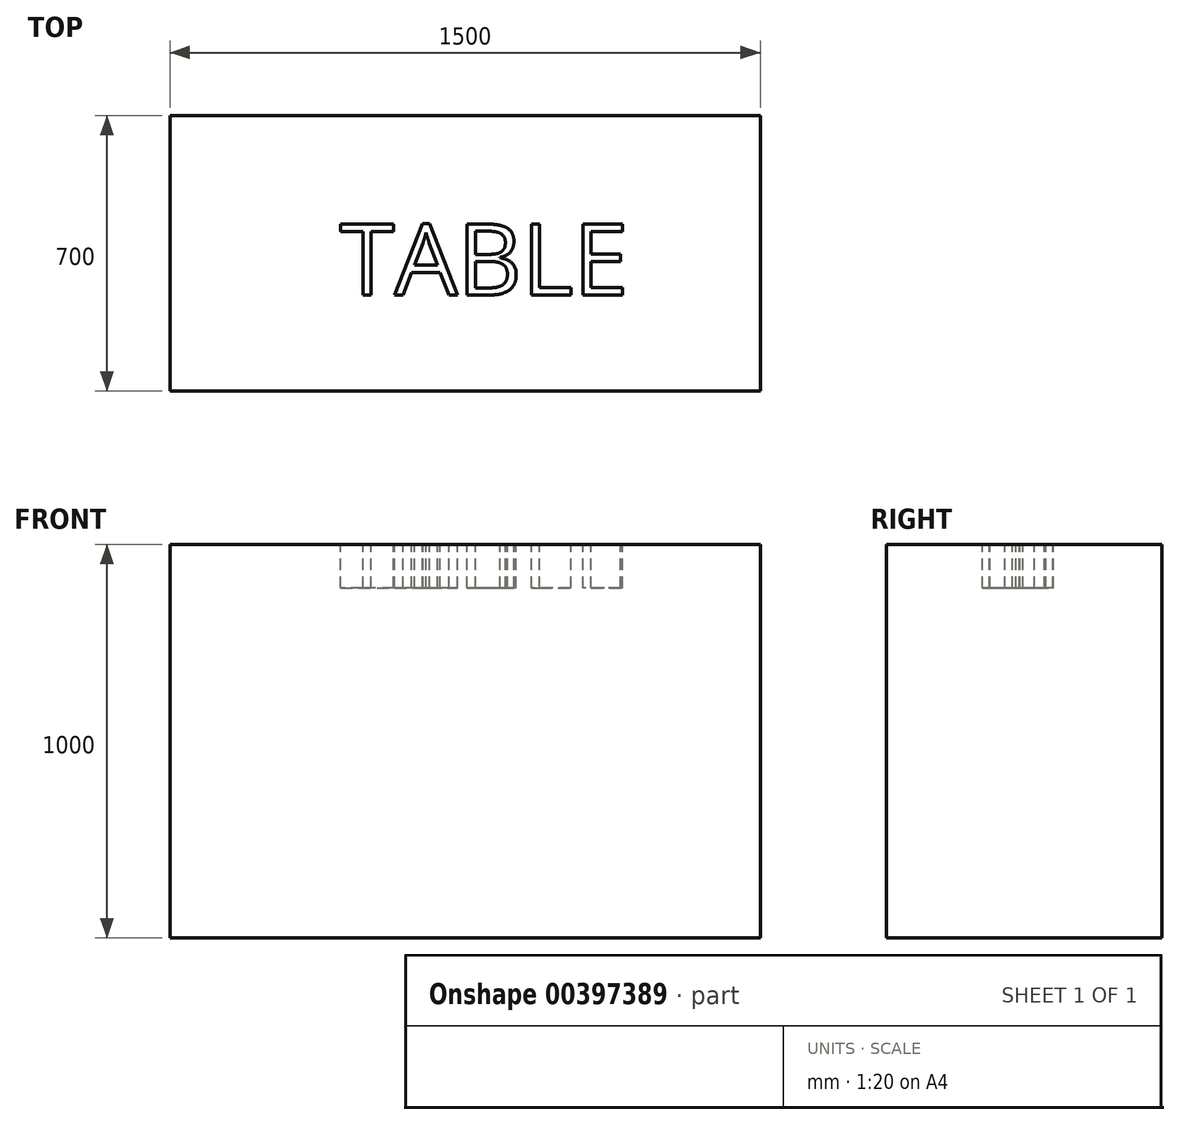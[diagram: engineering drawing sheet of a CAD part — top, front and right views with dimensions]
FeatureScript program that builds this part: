
annotation { "Feature Type Name" : "Feature", "Feature Type Description" : "" }
export const myFeature = defineFeature(function(context is Context, id is Id, definition is map)
    precondition{}
    {
        {
            var Q0;
            Q0=qCreatedBy(makeId("Top.planeOp"),FACE);
            var sketch = newSketch(context, id + "F0", { "sketchPlane" : qUnion([Q0])});
            skLineSegment(sketch, "E0.bottom", {"start": v(-19.1, 693.58) * mm, "end": v(1480.9, 693.58) * mm});
            skLineSegment(sketch, "E0.top", {"start": v(-19.1, -6.42) * mm, "end": v(1480.9, -6.42) * mm});
            skLineSegment(sketch, "E0.left", {"start": v(-19.1, 693.58) * mm, "end": v(-19.1, -6.42) * mm});
            skLineSegment(sketch, "E0.right", {"start": v(1480.9, 693.58) * mm, "end": v(1480.9, -6.42) * mm});
            skSolve(sketch);
        }
        {
            var Q0;
            Q0 = qSketchRegion(id + "F0", true);
            extrude(context, id + "F1", {"entities" : qUnion([Q0]), "depth" : 1000 * mm});
        }
        {
            var Q0;
            Q0=makeQuery(id+"F1.opExtrude","CAP_FACE",FACE,{"disambiguationData":[OSD([sQuery(id+"F0.wireOp",EDGE,"E0.bottom"),sQuery(id+"F0.wireOp",EDGE,"E0.top"),sQuery(id+"F0.wireOp",EDGE,"E0.left"),sQuery(id+"F0.wireOp",EDGE,"E0.right")])],"isStart":false});
            var sketch = newSketch(context, id + "F2", { "sketchPlane" : qUnion([Q0])});
            skText(sketch, "E1", { "text": "TABLE", "fontName": "OpenSans-Regular.ttf"});
            const initialGuessF2  = {"E1": [0.41256, 0.23772, 1, 0, 0.1815]};
            skSetInitialGuess(sketch, initialGuessF2);
            skSolve(sketch);
        }
        {
            var Q0;
            Q0 = qSketchRegion(id + "F2", true);
            extrude(context, id + "F3", {"entities" : qUnion([Q0]), "operationType" : NewBodyOperationType.REMOVE, "oppositeDirection" : true, "depth" : 111 * mm});
        }
    });
